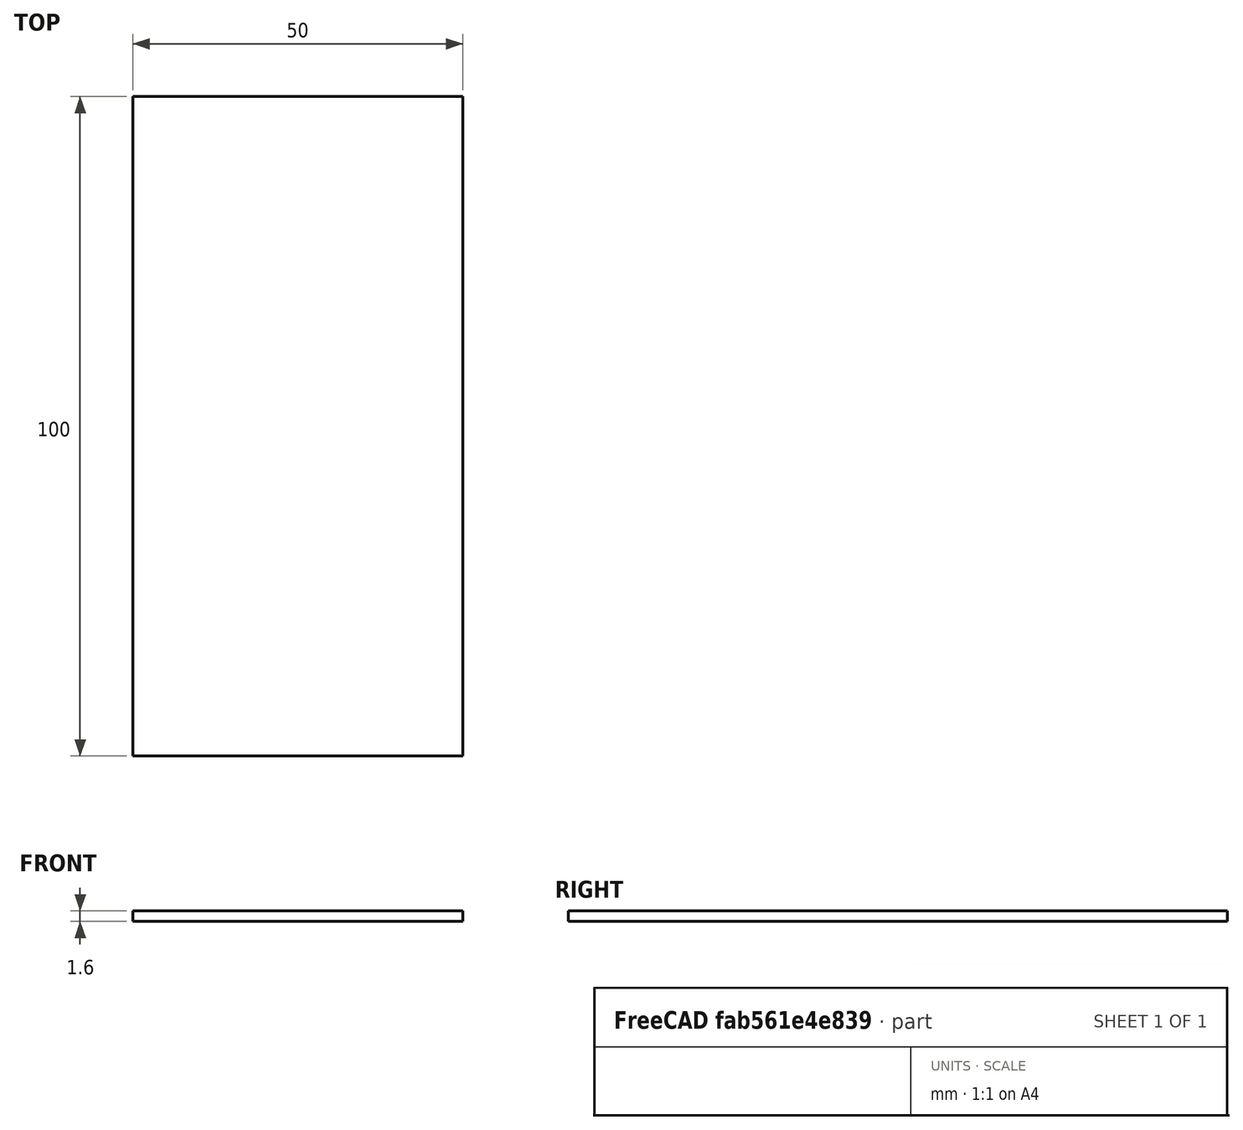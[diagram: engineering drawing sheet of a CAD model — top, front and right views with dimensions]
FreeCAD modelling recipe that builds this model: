
FCSTD DOCUMENT  (FreeCAD 0.20R29603 (Git))
Label: PCB_Main
License: All rights reserved
LicenseURL: http://en.wikipedia.org/wiki/All_rights_reserved
objects: Sketcher::SketchObject×1, PartDesign::Pad×1, PartDesign::Body×1
note: 4 computed .brp shape members not serialized (recipe doc carries the construction recipe); baked Part::Feature solids carry a one-line shape summary decoded from their .brp

FEATURE [Sketcher::SketchObject] Sketch
  FullyConstrained = true
  MapMode = 5
  Support = -> [XY_Plane]
  sketch-geometry (4):
    g0: LineSegment StartX=0 StartY=100 StartZ=0 EndX=50 EndY=100 EndZ=0
    g1: LineSegment StartX=50 StartY=100 StartZ=0 EndX=50 EndY=0 EndZ=0
    g2: LineSegment StartX=50 StartY=0 StartZ=0 EndX=0 EndY=0 EndZ=0
    g3: LineSegment StartX=0 StartY=0 StartZ=0 EndX=0 EndY=100 EndZ=0
  constraints (11):
    c: Coincident(g0,g1)
    c: Coincident(g1,g2)
    c: Coincident(g2,g3)
    c: Coincident(g3,g0)
    c: Horizontal(g0)
    c: Horizontal(g2)
    c: Vertical(g1)
    c: Vertical(g3)
    c: Coincident(g2,g-1)
    c: DistanceX(g2,g2) = 50
    c: DistanceY(g3,g3) = 100
FEATURE [PartDesign::Pad] Pad
  Direction = (0,0,1)
  Length = 1.6
  Length2 = 10
  Profile = -> Sketch
  ReferenceAxis = -> Sketch [N_Axis]
  Type = 0
FEATURE [PartDesign::Body] Body
  Group = -> [Sketch,Pad]
  Origin = -> Origin
  Tip = -> Pad
